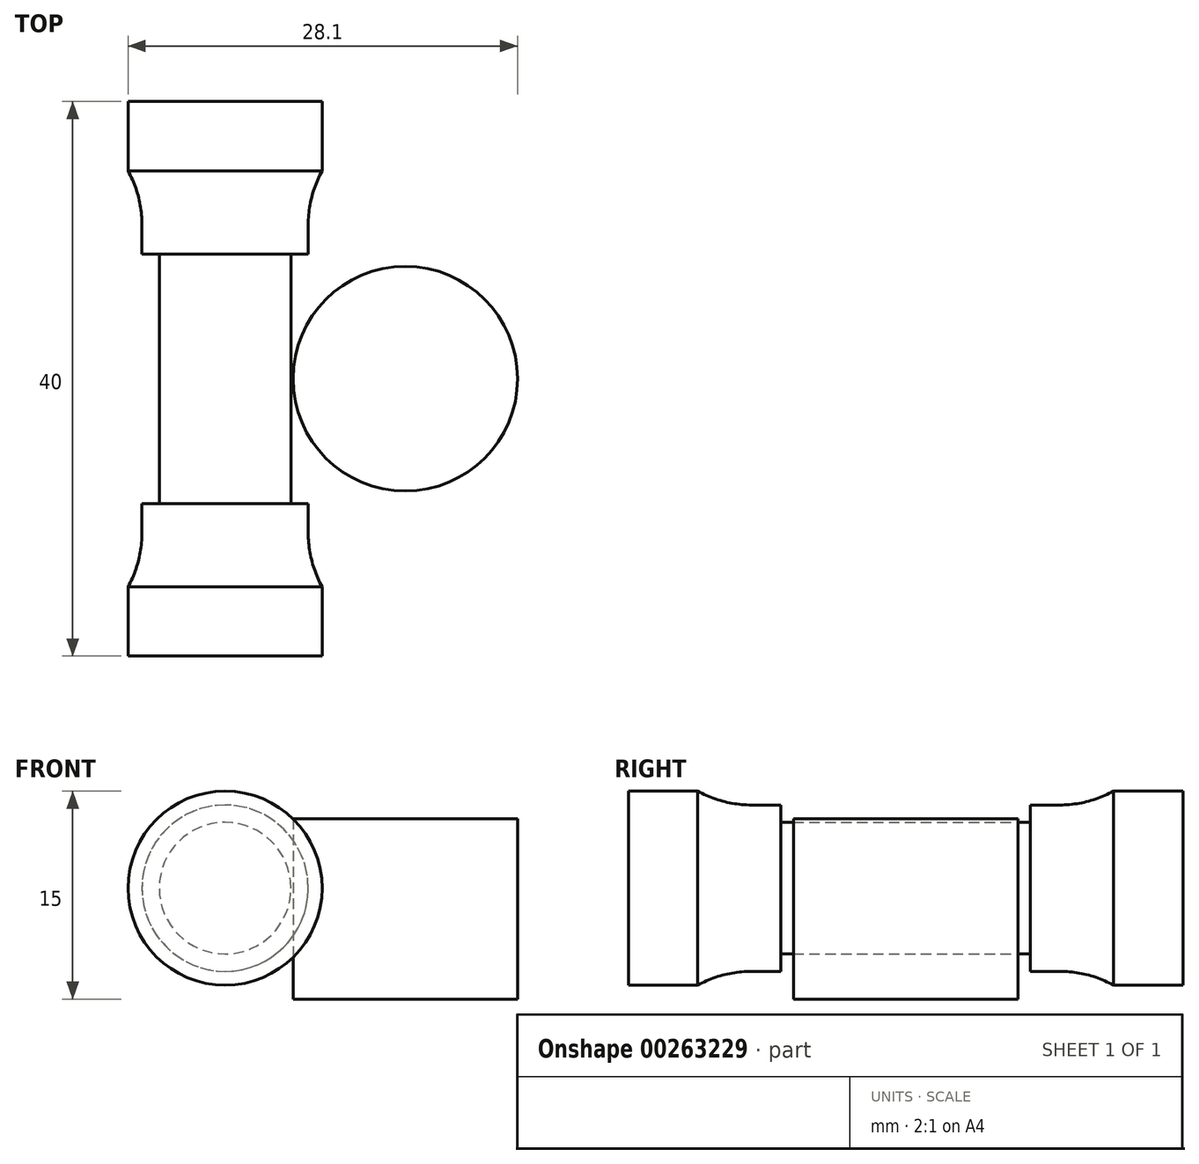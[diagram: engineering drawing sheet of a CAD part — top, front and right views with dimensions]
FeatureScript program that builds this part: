
annotation { "Feature Type Name" : "Feature", "Feature Type Description" : "" }
export const myFeature = defineFeature(function(context is Context, id is Id, definition is map)
    precondition{}
    {
        {
            var Q0;
            Q0=qCreatedBy(makeId("Top.planeOp"),FACE);
            var sketch = newSketch(context, id + "F0", { "sketchPlane" : qUnion([Q0])});
            skLineSegment(sketch, "E0.bottom", {"start": v(-18, 18) * mm, "end": v(18, 18) * mm, "construction": true});
            skLineSegment(sketch, "E0.top", {"start": v(-18, -18) * mm, "end": v(18, -18) * mm, "construction": true});
            skLineSegment(sketch, "E0.left", {"start": v(-18, 18) * mm, "end": v(-18, -18) * mm, "construction": true});
            skLineSegment(sketch, "E0.right", {"start": v(18, 18) * mm, "end": v(18, -18) * mm, "construction": true});
            skCircle(sketch, "E1", {"center": v(0, 0) * mm, "radius": 8 * mm, "construction": true});
            skLineSegment(sketch, "E2", {"start": v(-13, 18) * mm, "end": v(-13, -18) * mm, "construction": true});
            skLineSegment(sketch, "E3.bottom", {"start": v(-19, 15) * mm, "end": v(-7, 15) * mm, "construction": true});
            skLineSegment(sketch, "E3.top", {"start": v(-19, 9) * mm, "end": v(-7, 9) * mm, "construction": true});
            skLineSegment(sketch, "E3.left", {"start": v(-19, 15) * mm, "end": v(-19, 9) * mm, "construction": true});
            skLineSegment(sketch, "E3.right", {"start": v(-7, 15) * mm, "end": v(-7, 9) * mm, "construction": true});
            skLineSegment(sketch, "E4.bottom", {"start": v(-19, -9) * mm, "end": v(-7, -9) * mm, "construction": true});
            skLineSegment(sketch, "E4.top", {"start": v(-19, -15) * mm, "end": v(-7, -15) * mm, "construction": true});
            skLineSegment(sketch, "E4.left", {"start": v(-19, -9) * mm, "end": v(-19, -15) * mm, "construction": true});
            skLineSegment(sketch, "E4.right", {"start": v(-7, -9) * mm, "end": v(-7, -15) * mm, "construction": true});
            skLineSegment(sketch, "E5.bottom", {"start": v(-17, 52.94) * mm, "end": v(-9, 52.94) * mm, "construction": true});
            skLineSegment(sketch, "E5.top", {"start": v(-17, -59.52) * mm, "end": v(-9, -59.52) * mm, "construction": true});
            skLineSegment(sketch, "E5.left", {"start": v(-17, 52.94) * mm, "end": v(-17, -59.52) * mm, "construction": true});
            skLineSegment(sketch, "E5.right", {"start": v(-9, 52.94) * mm, "end": v(-9, -59.52) * mm, "construction": true});
            skSolve(sketch);
        }
        {
            var Q0;
            Q0=qCreatedBy(makeId("Top.planeOp"),FACE);
            cPlane(context, id + "F1", {"entities" : qUnion([Q0]), "cplaneType" : CPlaneType.OFFSET, "offset" : 8 * mm, "width" : 150 * mm, "height" : 150 * mm});
        }
        {
            var Q0;
            Q0=qCreatedBy(id+"F1.planeOp",FACE);
            var sketch = newSketch(context, id + "F2", { "sketchPlane" : qUnion([Q0])});
            skLineSegment(sketch, "E6", {"start": v(-13, 27) * mm, "end": v(-13, -24.88) * mm, "construction": true});
            skLineSegment(sketch, "E7", {"start": v(-17, 25.06) * mm, "end": v(-17, -25.9) * mm, "construction": true});
            skLineSegment(sketch, "E8", {"start": v(-19, 15) * mm, "end": v(-19, 9) * mm});
            skLineSegment(sketch, "E9", {"start": v(-19, 9) * mm, "end": v(-17.75, 9) * mm});
            skLineSegment(sketch, "E10", {"start": v(-17.75, 9) * mm, "end": v(-17.75, -9) * mm});
            skLineSegment(sketch, "E11", {"start": v(-17.75, -9) * mm, "end": v(-19, -9) * mm});
            skLineSegment(sketch, "E12", {"start": v(-19, -9) * mm, "end": v(-19, -15) * mm});
            skLineSegment(sketch, "E13", {"start": v(-19, 15) * mm, "end": v(-20, 15) * mm});
            skLineSegment(sketch, "E14", {"start": v(-20, 15) * mm, "end": v(-20, 20) * mm});
            skLineSegment(sketch, "E15", {"start": v(-20, 20) * mm, "end": v(-13, 20) * mm});
            skLineSegment(sketch, "E16", {"start": v(-13, 20) * mm, "end": v(-13, -20) * mm});
            skLineSegment(sketch, "E17", {"start": v(-13, -20) * mm, "end": v(-20, -20) * mm});
            skLineSegment(sketch, "E18", {"start": v(-20, -20) * mm, "end": v(-20, -15) * mm});
            skLineSegment(sketch, "E19", {"start": v(-20, -15) * mm, "end": v(-19, -15) * mm});
            skSolve(sketch);
        }
        {
            var Q0;
            Q0=makeQuery(id+"F2.imprint","IMPRINT",FACE,{"disambiguationData":[TD([[makeQuery(id+"F2.imprint","IMPRINT",EDGE,{"derivedFrom":sQuery(id+"F2.wireOp",EDGE,"E8")}),1.0]])]});
            var Q1;
            Q1=sQuery(id+"F2.wireOp",EDGE,"E6");
            revolve(context, id + "F3", {"entities" : qUnion([Q0]), "axis" : qUnion([Q1]), "revolveType" : RevolveType.FULL});
        }
        {
            var Q0;
            Q0=qCreatedBy(makeId("Top.planeOp"),FACE);
            var sketch = newSketch(context, id + "F4", { "sketchPlane" : qUnion([Q0])});
            skCircle(sketch, "E20", {"center": v(0, 0) * mm, "radius": 8.1 * mm});
            skSolve(sketch);
        }
        {
            var Q0;
            Q0=makeQuery(id+"F4.imprint","IMPRINT",FACE,{"disambiguationData":[TD([[makeQuery(id+"F4.imprint","IMPRINT",EDGE,{"derivedFrom":sQuery(id+"F4.wireOp",EDGE,"E20")}),1.0]])]});
            extrude(context, id + "F5", {"entities" : qUnion([Q0]), "depth" : 13 * mm});
        }
        {
            var Q0;
            Q0=makeQuery(id+"F3.opRevolve","SWEPT_EDGE",EDGE,{"disambiguationData":[OSD([sQuery(id+"F2.wireOp",EDGE,"E8"),sQuery(id+"F2.wireOp",EDGE,"E13")])]});
            var Q1;
            Q1=makeQuery(id+"F3.opRevolve","SWEPT_EDGE",EDGE,{"disambiguationData":[OSD([sQuery(id+"F2.wireOp",EDGE,"E12"),sQuery(id+"F2.wireOp",EDGE,"E19")])]});
            fillet(context, id + "F6", {"entities" : qUnion([Q0, Q1]), "radius" : 8 * mm, "tangentPropagation" : true, "allowEdgeOverflow" : false});
        }
    });
